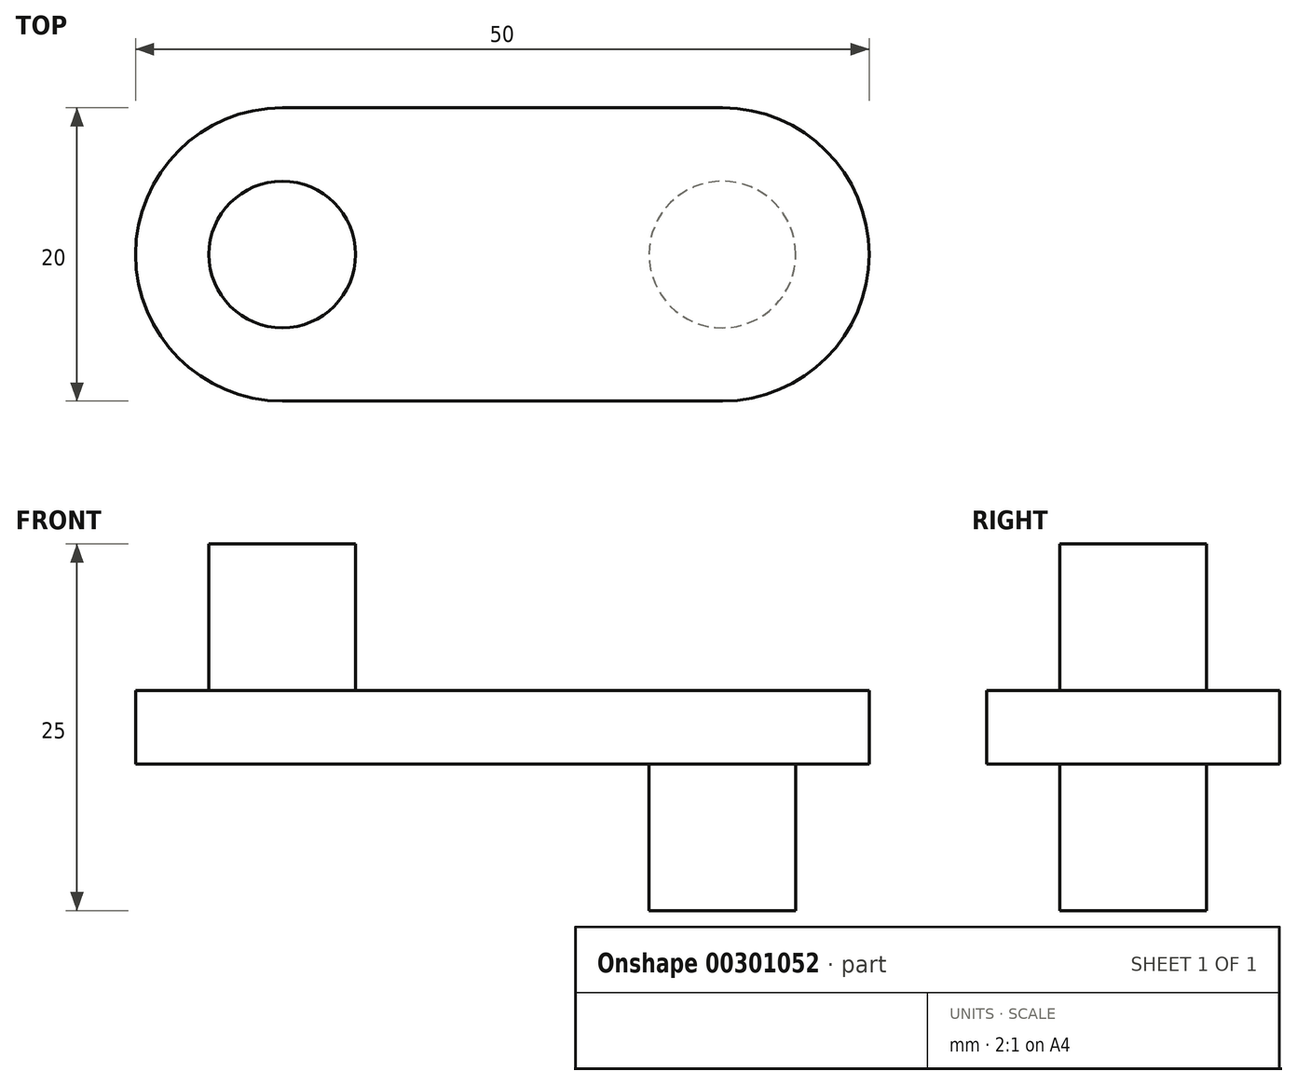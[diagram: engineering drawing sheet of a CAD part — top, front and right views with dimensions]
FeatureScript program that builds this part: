
annotation { "Feature Type Name" : "Feature", "Feature Type Description" : "" }
export const myFeature = defineFeature(function(context is Context, id is Id, definition is map)
    precondition{}
    {
        {
            var Q0;
            Q0=qCreatedBy(makeId("Top.planeOp"),FACE);
            var sketch = newSketch(context, id + "F0", { "sketchPlane" : qUnion([Q0])});
            skLineSegment(sketch, "E0", {"start": v(-30, 0) * mm, "end": v(0, 0) * mm});
            skLineSegment(sketch, "E1.MirrorCS", {"start": v(-30, -20) * mm, "end": v(0, -20) * mm});
            skArc(sketch, "E2", {"start": v(-30, 0) * mm, "mid": v(-40, -10) * mm, "end": v(-30, -20) * mm});
            skArc(sketch, "E3", {"start": v(0, 0) * mm, "mid": v(10, -10) * mm, "end": v(0, -20) * mm});
            skSolve(sketch);
        }
        {
            var Q0;
            Q0 = qSketchRegion(id + "F0", true);
            extrude(context, id + "F1", {"entities" : qUnion([Q0]), "endBound" : BoundingType.SYMMETRIC, "depth" : 5 * mm});
        }
        {
            var Q0;
            Q0=makeQuery(id+"F1.opExtrude","CAP_FACE",FACE,{"disambiguationData":[OSD([sQuery(id+"F0.wireOp",EDGE,"E0"),sQuery(id+"F0.wireOp",EDGE,"VerCj0QU-y6kP-9FSj-4a56-PNqR6XGnOSbt"),sQuery(id+"F0.wireOp",EDGE,"BF8I9aON-bstb-jMCr-h6v0-UmIwN5ducMgD"),sQuery(id+"F0.wireOp",EDGE,"E1.MirrorCS"),sQuery(id+"F0.wireOp",EDGE,"a7dcacd1-aa86-4882-897a-65ecb3f4d9470.MirrorCS"),sQuery(id+"F0.wireOp",EDGE,"2e34642d-99c6-4bc0-8820-2f5f5f6bf99d0.MirrorCS")])],"isStart":false});
            var sketch = newSketch(context, id + "F2", { "sketchPlane" : qUnion([Q0])});
            skCircle(sketch, "E4", {"center": v(-30, -10) * mm, "radius": 5 * mm});
            skSolve(sketch);
        }
        {
            var Q0;
            Q0 = qSketchRegion(id + "F2", true);
            extrude(context, id + "F3", {"entities" : qUnion([Q0]), "operationType" : NewBodyOperationType.ADD, "depth" : 10 * mm});
        }
        {
            var Q0;
            Q0=makeQuery(id+"F1.opExtrude","CAP_FACE",FACE,{"disambiguationData":[OSD([sQuery(id+"F0.wireOp",EDGE,"E0"),sQuery(id+"F0.wireOp",EDGE,"E1.MirrorCS"),sQuery(id+"F0.wireOp",EDGE,"E2"),sQuery(id+"F0.wireOp",EDGE,"E3")])],"isStart":true});
            var sketch = newSketch(context, id + "F4", { "sketchPlane" : qUnion([Q0])});
            skCircle(sketch, "E5", {"center": v(0, 10) * mm, "radius": 5 * mm});
            skSolve(sketch);
        }
        {
            var Q0;
            Q0 = qSketchRegion(id + "F4", true);
            extrude(context, id + "F5", {"entities" : qUnion([Q0]), "operationType" : NewBodyOperationType.ADD, "depth" : 10 * mm});
        }
    });
